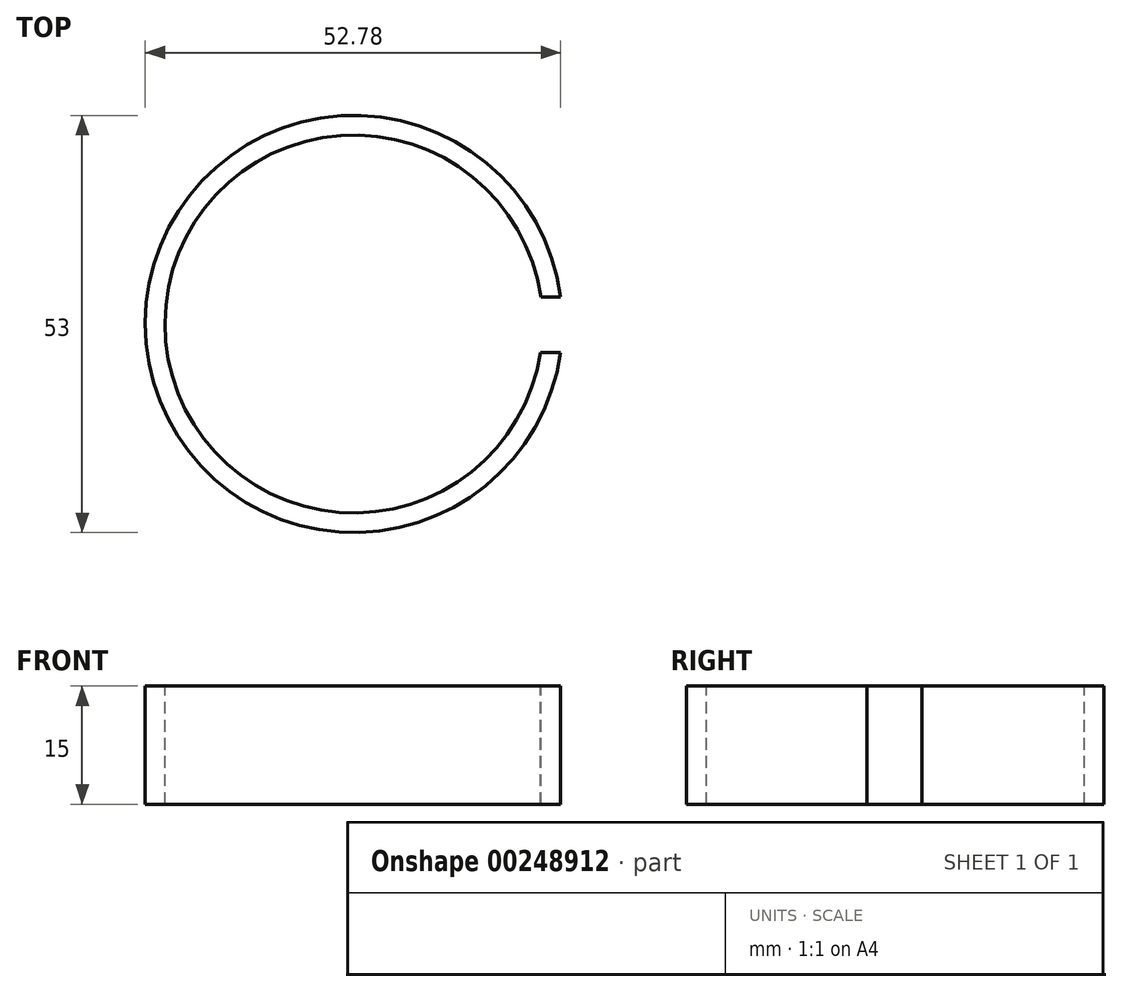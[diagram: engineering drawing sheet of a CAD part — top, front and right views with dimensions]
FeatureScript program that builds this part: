
annotation { "Feature Type Name" : "Feature", "Feature Type Description" : "" }
export const myFeature = defineFeature(function(context is Context, id is Id, definition is map)
    precondition{}
    {
        {
            var Q0;
            Q0=qCreatedBy(makeId("Top.planeOp"),FACE);
            var sketch = newSketch(context, id + "F0", { "sketchPlane" : qUnion([Q0])});
            skCircle(sketch, "E0", {"center": v(0, 0) * mm, "radius": 26.5 * mm});
            skSolve(sketch);
        }
        {
            var Q0;
            Q0=makeQuery(id+"F0.imprint","IMPRINT",FACE,{"disambiguationData":[TD([[makeQuery(id+"F0.imprint","IMPRINT",EDGE,{"derivedFrom":sQuery(id+"F0.wireOp",EDGE,"E0")}),1.0]])]});
            extrude(context, id + "F1", {"entities" : qUnion([Q0]), "depth" : 15 * mm});
        }
        {
            var Q0;
            Q0=makeQuery(id+"F1.opExtrude","CAP_FACE",FACE,{"disambiguationData":[OSD([sQuery(id+"F0.wireOp",EDGE,"E0")])],"isStart":false});
            var sketch = newSketch(context, id + "F2", { "sketchPlane" : qUnion([Q0])});
            skPoint(sketch, "E1", {"position": v(0, 0) * mm});
            skSolve(sketch);
        }
        {
            var Q0;
            Q0=sQuery(id+"F2.wireOp",VERTEX,"E1");
            var Q1;
            Q1=makeQuery(id+"F1.opExtrude","SWEPT_BODY",BODY,{"disambiguationData":[OSD([sQuery(id+"F0.wireOp",EDGE,"E0")])]});
            hole(context, id + "F3", {"style" : HoleStyle.SIMPLE, "endStyle" : HoleEndStyle.THROUGH, "holeDiameter" : 48 * mm, "tappedDepth" : 12 * mm, "tapClearance" : 3, "locations" : qUnion([Q0]), "scope" : qUnion([Q1])});
        }
        {
            var Q0;
            Q0=makeQuery(id+"F1.opExtrude","CAP_FACE",FACE,{"disambiguationData":[OSD([sQuery(id+"F0.wireOp",EDGE,"E0")])],"isStart":false});
            var sketch = newSketch(context, id + "F4", { "sketchPlane" : qUnion([Q0])});
            skLineSegment(sketch, "E2", {"start": v(23.76, 3.4) * mm, "end": v(26.28, 3.4) * mm});
            skLineSegment(sketch, "E3", {"start": v(23.73, -3.6) * mm, "end": v(26.25, -3.6) * mm});
            skSolve(sketch);
        }
        {
            var Q0;
            {var subQ0=sQuery(id+"F4.wireOp",EDGE,"E2");Q0=makeQuery(id+"F4.imprint","IMPRINT",FACE,{"disambiguationData":[TD([[makeQuery(id+"F4.imprint","IMPRINT",EDGE,{"derivedFrom":subQ0}),-1.0]])]});}
            extrude(context, id + "F5", {"entities" : qUnion([Q0]), "operationType" : NewBodyOperationType.REMOVE, "endBound" : BoundingType.THROUGH_ALL, "oppositeDirection" : true, "depth" : 25 * mm});
        }
    });
